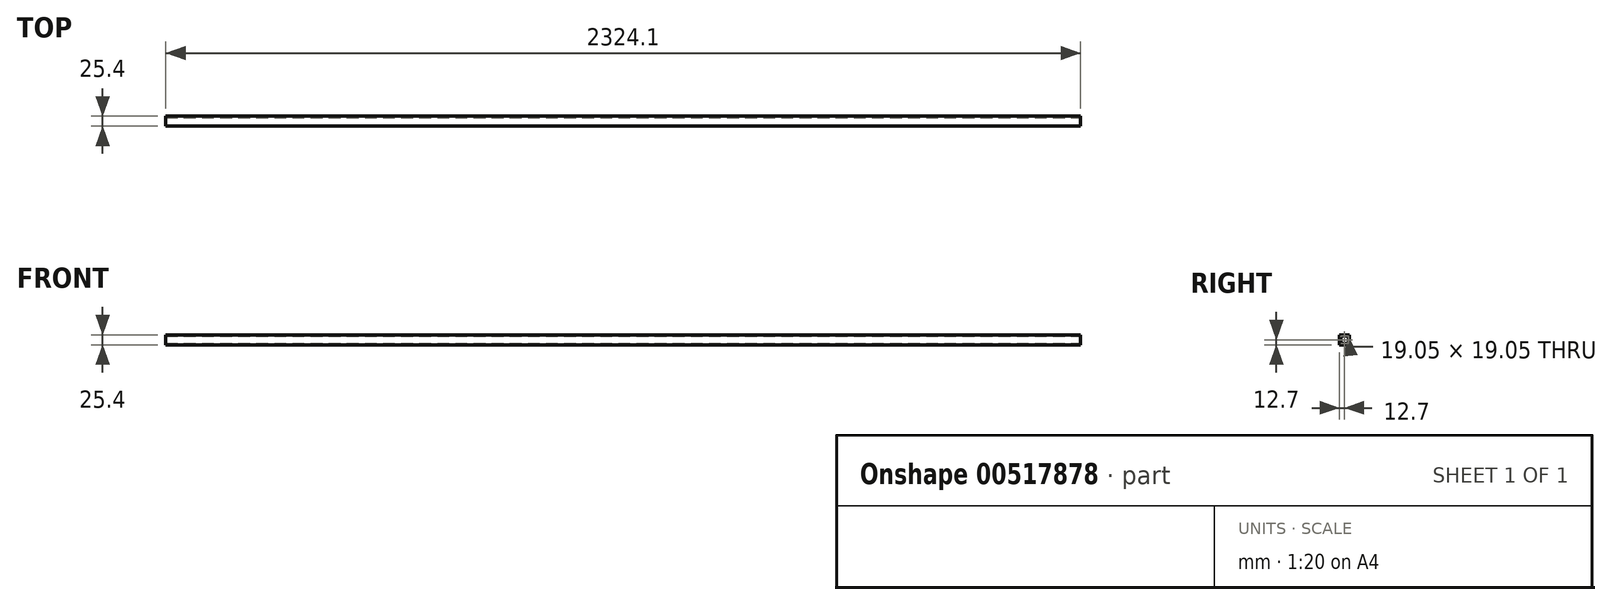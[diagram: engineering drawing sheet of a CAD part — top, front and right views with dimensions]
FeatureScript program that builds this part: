
annotation { "Feature Type Name" : "Feature", "Feature Type Description" : "" }
export const myFeature = defineFeature(function(context is Context, id is Id, definition is map)
    precondition{}
    {
        {
            var Q0;
            Q0=qCreatedBy(makeId("Right.planeOp"),FACE);
            var sketch = newSketch(context, id + "F0", { "sketchPlane" : qUnion([Q0])});
            skLineSegment(sketch, "E0.bottom", {"start": v(0, 0) * mm, "end": v(25.4, 0) * mm});
            skLineSegment(sketch, "E0.top", {"start": v(0, 25.4) * mm, "end": v(25.4, 25.4) * mm});
            skLineSegment(sketch, "E0.left", {"start": v(0, 0) * mm, "end": v(0, 25.4) * mm});
            skLineSegment(sketch, "E0.right", {"start": v(25.4, 0) * mm, "end": v(25.4, 25.4) * mm});
            skLineSegment(sketch, "E1.0", {"start": v(3.17, 22.22) * mm, "end": v(22.22, 22.22) * mm});
            skLineSegment(sketch, "E1.1", {"start": v(3.17, 3.18) * mm, "end": v(3.17, 22.23) * mm});
            skLineSegment(sketch, "E1.2", {"start": v(3.18, 3.18) * mm, "end": v(22.22, 3.18) * mm});
            skLineSegment(sketch, "E1.3", {"start": v(22.22, 3.18) * mm, "end": v(22.22, 22.22) * mm});
            skSolve(sketch);
        }
        {
            var Q0;
            Q0 = qSketchRegion(id + "F0", true);
            extrude(context, id + "F1", {"entities" : qUnion([Q0]), "oppositeDirection" : true, "depth" : 2324.1 * mm, "offsetDistance" : 25.4 * mm});
        }
    });
